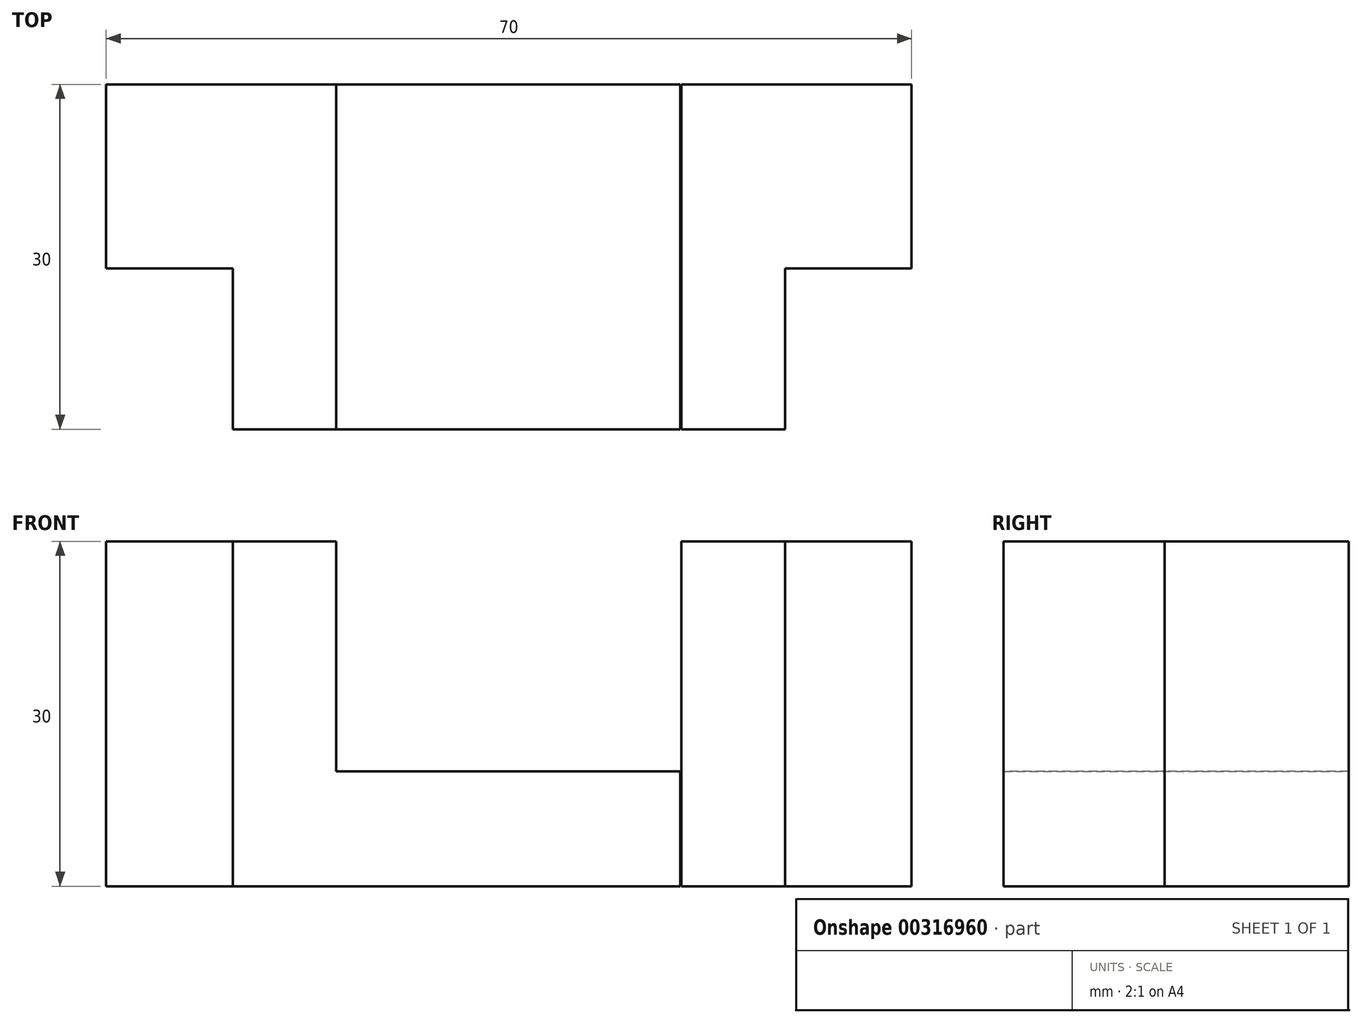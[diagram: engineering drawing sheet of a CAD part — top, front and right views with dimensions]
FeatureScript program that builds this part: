
annotation { "Feature Type Name" : "Feature", "Feature Type Description" : "" }
export const myFeature = defineFeature(function(context is Context, id is Id, definition is map)
    precondition{}
    {
        {
            var Q0;
            Q0=qCreatedBy(makeId("Top.planeOp"),FACE);
            var sketch = newSketch(context, id + "F0", { "sketchPlane" : qUnion([Q0])});
            skLineSegment(sketch, "E0", {"start": v(-38.6, 21.4) * mm, "end": v(31.4, 21.4) * mm});
            skLineSegment(sketch, "E1", {"start": v(-38.6, 21.4) * mm, "end": v(-38.6, 5.4) * mm});
            skLineSegment(sketch, "E2", {"start": v(-38.6, 5.4) * mm, "end": v(-27.6, 5.4) * mm});
            skLineSegment(sketch, "E3", {"start": v(-27.6, 5.4) * mm, "end": v(-27.6, -8.6) * mm});
            skLineSegment(sketch, "E4", {"start": v(-27.6, -8.6) * mm, "end": v(20.4, -8.6) * mm});
            skLineSegment(sketch, "E5", {"start": v(20.4, -8.6) * mm, "end": v(20.4, 5.4) * mm});
            skLineSegment(sketch, "E6", {"start": v(20.4, 5.4) * mm, "end": v(31.4, 5.4) * mm});
            skLineSegment(sketch, "E7", {"start": v(31.4, 21.4) * mm, "end": v(31.4, 5.4) * mm});
            skLineSegment(sketch, "E8", {"start": v(-18.6, 21.4) * mm, "end": v(-18.6, -8.6) * mm});
            skLineSegment(sketch, "E9", {"start": v(11.4, 21.4) * mm, "end": v(11.4, -8.6) * mm});
            skSolve(sketch);
        }
        {
            var Q0;
            {var subQ0=sQuery(id+"F0.wireOp",EDGE,"E1");Q0=makeQuery(id+"F0.imprint","IMPRINT",FACE,{"disambiguationData":[TD([[makeQuery(id+"F0.imprint","IMPRINT",EDGE,{"derivedFrom":subQ0}),1.0]])]});}
            var Q1;
            {var subQ0=sQuery(id+"F0.wireOp",EDGE,"E5");Q1=makeQuery(id+"F0.imprint","IMPRINT",FACE,{"disambiguationData":[TD([[makeQuery(id+"F0.imprint","IMPRINT",EDGE,{"derivedFrom":subQ0}),1.0]])]});}
            extrude(context, id + "F1", {"entities" : qUnion([Q0, Q1]), "depth" : 30 * mm});
        }
        {
            var Q0;
            Q0=qCreatedBy(makeId("Front.planeOp"),FACE);
            var sketch = newSketch(context, id + "F2", { "sketchPlane" : qUnion([Q0])});
            skLineSegment(sketch, "E10", {"start": v(-18.72, 10) * mm, "end": v(11.28, 10) * mm});
            skLineSegment(sketch, "E11", {"start": v(-18.72, 10) * mm, "end": v(-18.72, 0) * mm});
            skLineSegment(sketch, "E12", {"start": v(-18.72, 0) * mm, "end": v(11.28, 0) * mm});
            skLineSegment(sketch, "E13", {"start": v(11.28, 0) * mm, "end": v(11.28, 10) * mm});
            skSolve(sketch);
        }
        {
            var Q0;
            Q0=makeQuery(id+"F2.imprint","IMPRINT",FACE,{"disambiguationData":[TD([[makeQuery(id+"F2.imprint","IMPRINT",EDGE,{"derivedFrom":sQuery(id+"F2.wireOp",EDGE,"E10")}),-1.0]])]});
            extrude(context, id + "F3", {"entities" : qUnion([Q0]), "operationType" : NewBodyOperationType.ADD, "oppositeDirection" : true, "depth" : 21.4 * mm});
        }
        {
            var Q0;
            Q0=makeQuery(id+"F3.opExtrude","CAP_FACE",FACE,{"disambiguationData":[OSD([sQuery(id+"F2.wireOp",EDGE,"E10"),sQuery(id+"F2.wireOp",EDGE,"E11"),sQuery(id+"F2.wireOp",EDGE,"E12"),sQuery(id+"F2.wireOp",EDGE,"E13")])],"isStart":true});
            extrude(context, id + "F4", {"entities" : qUnion([Q0]), "operationType" : NewBodyOperationType.ADD, "depth" : 8.6 * mm});
        }
    });
